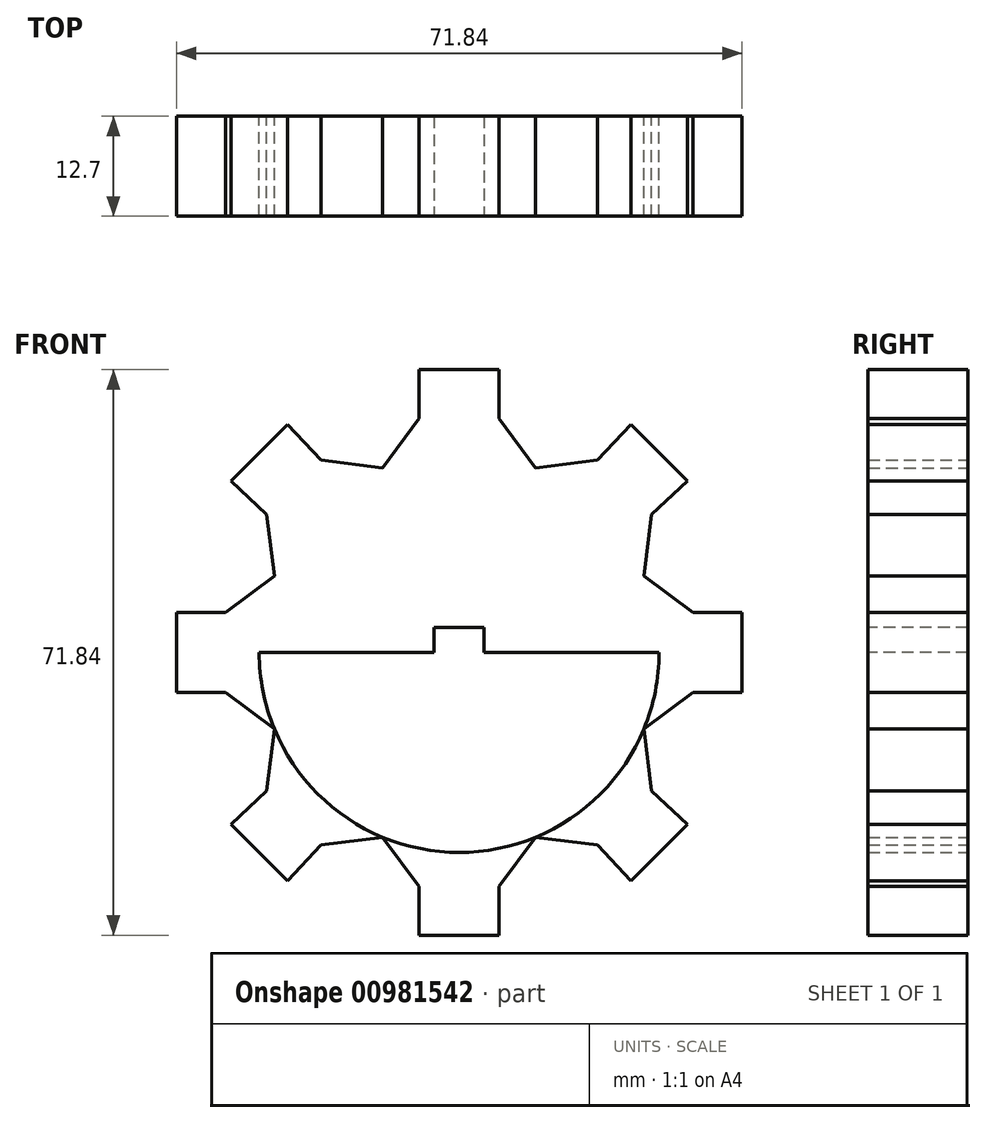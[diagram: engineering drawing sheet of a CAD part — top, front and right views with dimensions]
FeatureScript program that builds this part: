
annotation { "Feature Type Name" : "Feature", "Feature Type Description" : "" }
export const myFeature = defineFeature(function(context is Context, id is Id, definition is map)
    precondition{}
    {
        {
            var Q0;
            Q0=qCreatedBy(makeId("Front.planeOp"),FACE);
            var sketch = newSketch(context, id + "F0", { "sketchPlane" : qUnion([Q0])});
            skCircle(sketch, "E0", {"center": v(0, 0) * mm, "radius": 25.4 * mm});
            skLineSegment(sketch, "E1.bottom", {"start": v(0, 0) * mm, "end": v(-25.4, 0) * mm});
            skLineSegment(sketch, "E1.left", {"start": v(0, 0) * mm, "end": v(0, 25.4) * mm});
            skLineSegment(sketch, "E2", {"start": v(-25.4, 0) * mm, "end": v(-35.92, 0) * mm});
            skLineSegment(sketch, "E3", {"start": v(0, 25.4) * mm, "end": v(0, 35.92) * mm});
            skLineSegment(sketch, "E4", {"start": v(0, 35.92) * mm, "end": v(-5.08, 35.92) * mm});
            skPoint(sketch, "E5.endSnap0", {"position": v(-5.08, 29.7) * mm});
            skLineSegment(sketch, "E6", {"start": v(-25.4, 25.4) * mm, "end": v(-21.8, 29) * mm});
            skLineSegment(sketch, "E7", {"start": v(-21.8, 29) * mm, "end": v(-17.56, 24.43) * mm});
            skLineSegment(sketch, "E8", {"start": v(-25.4, 25.4) * mm, "end": v(-29, 21.8) * mm});
            skLineSegment(sketch, "E9", {"start": v(-29, 21.8) * mm, "end": v(-24.43, 17.56) * mm});
            skLineSegment(sketch, "E10", {"start": v(-35.92, 0) * mm, "end": v(-35.92, 5.08) * mm});
            skLineSegment(sketch, "E11", {"start": v(-35.92, 5.08) * mm, "end": v(-29.7, 5.08) * mm});
            skPoint(sketch, "E11.endSnap0", {"position": v(-29.7, 4.86) * mm});
            skLineSegment(sketch, "E12", {"start": v(-9.72, 23.47) * mm, "end": v(-17.56, 24.43) * mm});
            skLineSegment(sketch, "E13", {"start": v(-24.43, 17.56) * mm, "end": v(-23.47, 9.72) * mm});
            skLineSegment(sketch, "E14", {"start": v(-9.72, 23.47) * mm, "end": v(-5.08, 29.7) * mm});
            skLineSegment(sketch, "E15", {"start": v(-5.08, 29.7) * mm, "end": v(-5.08, 35.92) * mm});
            skLineSegment(sketch, "E16", {"start": v(-23.47, 9.72) * mm, "end": v(-29.7, 5.08) * mm});
            skLineSegment(sketch, "E17.1.0", {"start": v(25.4, 0) * mm, "end": v(35.92, 0) * mm});
            skLineSegment(sketch, "E17.1.1", {"start": v(23.47, 9.72) * mm, "end": v(24.43, 17.56) * mm});
            skLineSegment(sketch, "E17.1.2", {"start": v(35.92, 0) * mm, "end": v(35.92, 5.08) * mm});
            skLineSegment(sketch, "E17.1.3", {"start": v(9.72, 23.47) * mm, "end": v(5.08, 29.7) * mm});
            skLineSegment(sketch, "E17.1.4", {"start": v(17.56, 24.43) * mm, "end": v(9.72, 23.47) * mm});
            skLineSegment(sketch, "E17.1.5", {"start": v(29, 21.8) * mm, "end": v(24.43, 17.56) * mm});
            skLineSegment(sketch, "E17.1.6", {"start": v(29.7, 5.08) * mm, "end": v(35.92, 5.08) * mm});
            skLineSegment(sketch, "E17.1.7", {"start": v(23.47, 9.72) * mm, "end": v(29.7, 5.08) * mm});
            skPoint(sketch, "E17.1.8", {"position": v(4.86, 29.7) * mm});
            skLineSegment(sketch, "E17.1.10", {"start": v(0, 0) * mm, "end": v(25.4, 0) * mm});
            skLineSegment(sketch, "E17.1.11", {"start": v(5.08, 35.92) * mm, "end": v(5.08, 29.7) * mm});
            skPoint(sketch, "E17.1.12", {"position": v(29.7, 5.08) * mm});
            skLineSegment(sketch, "E17.1.13", {"start": v(21.8, 29) * mm, "end": v(17.56, 24.43) * mm});
            skLineSegment(sketch, "E17.1.15", {"start": v(25.4, 25.4) * mm, "end": v(29, 21.8) * mm});
            skLineSegment(sketch, "E17.1.16", {"start": v(0, 35.92) * mm, "end": v(5.08, 35.92) * mm});
            skLineSegment(sketch, "E17.1.17", {"start": v(25.4, 25.4) * mm, "end": v(21.8, 29) * mm});
            skLineSegment(sketch, "E17.2.0", {"start": v(0, -25.4) * mm, "end": v(0, -35.92) * mm});
            skLineSegment(sketch, "E17.2.1", {"start": v(9.72, -23.47) * mm, "end": v(17.56, -24.43) * mm});
            skLineSegment(sketch, "E17.2.2", {"start": v(0, -35.92) * mm, "end": v(5.08, -35.92) * mm});
            skLineSegment(sketch, "E17.2.3", {"start": v(23.47, -9.72) * mm, "end": v(29.7, -5.08) * mm});
            skLineSegment(sketch, "E17.2.4", {"start": v(24.43, -17.56) * mm, "end": v(23.47, -9.72) * mm});
            skLineSegment(sketch, "E17.2.5", {"start": v(21.8, -29) * mm, "end": v(17.56, -24.43) * mm});
            skLineSegment(sketch, "E17.2.6", {"start": v(5.08, -29.7) * mm, "end": v(5.08, -35.92) * mm});
            skLineSegment(sketch, "E17.2.7", {"start": v(9.72, -23.47) * mm, "end": v(5.08, -29.7) * mm});
            skPoint(sketch, "E17.2.8", {"position": v(29.7, -4.86) * mm});
            skLineSegment(sketch, "E17.2.9", {"start": v(0, 0) * mm, "end": v(25.4, 0) * mm});
            skLineSegment(sketch, "E17.2.10", {"start": v(0, 0) * mm, "end": v(0, -25.4) * mm});
            skLineSegment(sketch, "E17.2.11", {"start": v(35.92, -5.08) * mm, "end": v(29.7, -5.08) * mm});
            skPoint(sketch, "E17.2.12", {"position": v(5.08, -29.7) * mm});
            skLineSegment(sketch, "E17.2.13", {"start": v(29, -21.8) * mm, "end": v(24.43, -17.56) * mm});
            skLineSegment(sketch, "E17.2.14", {"start": v(25.4, 0) * mm, "end": v(35.92, 0) * mm});
            skLineSegment(sketch, "E17.2.15", {"start": v(25.4, -25.4) * mm, "end": v(21.8, -29) * mm});
            skLineSegment(sketch, "E17.2.16", {"start": v(35.92, 0) * mm, "end": v(35.92, -5.08) * mm});
            skLineSegment(sketch, "E17.2.17", {"start": v(25.4, -25.4) * mm, "end": v(29, -21.8) * mm});
            skLineSegment(sketch, "E17.3.1", {"start": v(-23.47, -9.72) * mm, "end": v(-24.43, -17.56) * mm});
            skLineSegment(sketch, "E17.3.2", {"start": v(-35.92, 0) * mm, "end": v(-35.92, -5.08) * mm});
            skLineSegment(sketch, "E17.3.3", {"start": v(-9.72, -23.47) * mm, "end": v(-5.08, -29.7) * mm});
            skLineSegment(sketch, "E17.3.4", {"start": v(-17.56, -24.43) * mm, "end": v(-9.72, -23.47) * mm});
            skLineSegment(sketch, "E17.3.5", {"start": v(-29, -21.8) * mm, "end": v(-24.43, -17.56) * mm});
            skLineSegment(sketch, "E17.3.6", {"start": v(-29.7, -5.08) * mm, "end": v(-35.92, -5.08) * mm});
            skLineSegment(sketch, "E17.3.7", {"start": v(-23.47, -9.72) * mm, "end": v(-29.7, -5.08) * mm});
            skPoint(sketch, "E17.3.8", {"position": v(-4.86, -29.7) * mm});
            skLineSegment(sketch, "E17.3.9", {"start": v(0, 0) * mm, "end": v(0, -25.4) * mm});
            skLineSegment(sketch, "E17.3.11", {"start": v(-5.08, -35.92) * mm, "end": v(-5.08, -29.7) * mm});
            skPoint(sketch, "E17.3.12", {"position": v(-29.7, -5.08) * mm});
            skLineSegment(sketch, "E17.3.13", {"start": v(-21.8, -29) * mm, "end": v(-17.56, -24.43) * mm});
            skLineSegment(sketch, "E17.3.14", {"start": v(0, -25.4) * mm, "end": v(0, -35.92) * mm});
            skLineSegment(sketch, "E17.3.15", {"start": v(-25.4, -25.4) * mm, "end": v(-29, -21.8) * mm});
            skLineSegment(sketch, "E17.3.16", {"start": v(0, -35.92) * mm, "end": v(-5.08, -35.92) * mm});
            skLineSegment(sketch, "E17.3.17", {"start": v(-25.4, -25.4) * mm, "end": v(-21.8, -29) * mm});
            skLineSegment(sketch, "E17.anchor1", {"start": v(0, 0) * mm, "end": v(-35.92, 0) * mm, "construction": true});
            skLineSegment(sketch, "E17.anchor2", {"start": v(0, 0) * mm, "end": v(0, -35.92) * mm, "construction": true});
            skSolve(sketch);
        }
        {
            var Q0;
            Q0=makeQuery(id+"F0.imprint","IMPRINT",FACE,{"disambiguationData":[TD([[makeQuery(id+"F0.imprint","IMPRINT",EDGE,{"derivedFrom":sQuery(id+"F0.wireOp",EDGE,"E4")}),1.0]])]});
            var Q1;
            {var subQ1=sQuery(id+"F0.wireOp",EDGE,"E17.1.3");Q1=makeQuery(id+"F0.imprint","IMPRINT",FACE,{"disambiguationData":[TD([[makeQuery(id+"F0.imprint","IMPRINT",EDGE,{"derivedFrom":subQ1}),1.0]])]});}
            var Q2;
            {var subQ1=sQuery(id+"F0.wireOp",EDGE,"E17.1.1");Q2=makeQuery(id+"F0.imprint","IMPRINT",FACE,{"disambiguationData":[TD([[makeQuery(id+"F0.imprint","IMPRINT",EDGE,{"derivedFrom":subQ1}),1.0]])]});}
            var Q3;
            Q3=makeQuery(id+"F0.imprint","IMPRINT",FACE,{"disambiguationData":[TD([[makeQuery(id+"F0.imprint","IMPRINT",EDGE,{"derivedFrom":sQuery(id+"F0.wireOp",EDGE,"E17.1.2")}),1.0]])]});
            var Q4;
            {var subQ1=sQuery(id+"F0.wireOp",EDGE,"E17.2.3");Q4=makeQuery(id+"F0.imprint","IMPRINT",FACE,{"disambiguationData":[TD([[makeQuery(id+"F0.imprint","IMPRINT",EDGE,{"derivedFrom":subQ1}),1.0]])]});}
            var Q5;
            {var subQ1=sQuery(id+"F0.wireOp",EDGE,"E17.2.1");Q5=makeQuery(id+"F0.imprint","IMPRINT",FACE,{"disambiguationData":[TD([[makeQuery(id+"F0.imprint","IMPRINT",EDGE,{"derivedFrom":subQ1}),1.0]])]});}
            var Q6;
            Q6=makeQuery(id+"F0.imprint","IMPRINT",FACE,{"disambiguationData":[TD([[makeQuery(id+"F0.imprint","IMPRINT",EDGE,{"derivedFrom":sQuery(id+"F0.wireOp",EDGE,"E17.2.2")}),1.0]])]});
            var Q7;
            {var subQ1=sQuery(id+"F0.wireOp",EDGE,"E17.3.3");Q7=makeQuery(id+"F0.imprint","IMPRINT",FACE,{"disambiguationData":[TD([[makeQuery(id+"F0.imprint","IMPRINT",EDGE,{"derivedFrom":subQ1}),1.0]])]});}
            var Q8;
            {var subQ1=sQuery(id+"F0.wireOp",EDGE,"E17.3.1");Q8=makeQuery(id+"F0.imprint","IMPRINT",FACE,{"disambiguationData":[TD([[makeQuery(id+"F0.imprint","IMPRINT",EDGE,{"derivedFrom":subQ1}),1.0]])]});}
            var Q9;
            {var subQ0=sQuery(id+"F0.wireOp",EDGE,"E2");Q9=makeQuery(id+"F0.imprint","IMPRINT",FACE,{"disambiguationData":[TD([[makeQuery(id+"F0.imprint","IMPRINT",EDGE,{"derivedFrom":subQ0}),1.0]])]});}
            var Q10;
            Q10=makeQuery(id+"F0.imprint","IMPRINT",FACE,{"disambiguationData":[TD([[makeQuery(id+"F0.imprint","IMPRINT",EDGE,{"derivedFrom":sQuery(id+"F0.wireOp",EDGE,"E10")}),-1.0]])]});
            var Q11;
            Q11=makeQuery(id+"F0.imprint","IMPRINT",FACE,{"disambiguationData":[TD([[makeQuery(id+"F0.imprint","IMPRINT",EDGE,{"derivedFrom":sQuery(id+"F0.wireOp",EDGE,"E6")}),-1.0]])]});
            var Q12;
            {var subQ0=sQuery(id+"F0.wireOp",EDGE,"E1.left");Q12=makeQuery(id+"F0.imprint","IMPRINT",FACE,{"disambiguationData":[TD([[makeQuery(id+"F0.imprint","IMPRINT",EDGE,{"derivedFrom":subQ0}),1.0]])]});}
            var Q13;
            {var subQ2=sQuery(id+"F0.wireOp",EDGE,"E1.left");Q13=makeQuery(id+"F0.imprint","IMPRINT",FACE,{"disambiguationData":[TD([[makeQuery(id+"F0.imprint","IMPRINT",EDGE,{"derivedFrom":subQ2}),-1.0]])]});}
            var Q14;
            {var subQ2=sQuery(id+"F0.wireOp",EDGE,"E17.2.9");Q14=makeQuery(id+"F0.imprint","IMPRINT",FACE,{"disambiguationData":[TD([[makeQuery(id+"F0.imprint","IMPRINT",EDGE,{"derivedFrom":subQ2}),-1.0]])]});}
            var Q15;
            {var subQ0=sQuery(id+"F0.wireOp",EDGE,"E17.3.9");Q15=makeQuery(id+"F0.imprint","IMPRINT",FACE,{"disambiguationData":[TD([[makeQuery(id+"F0.imprint","IMPRINT",EDGE,{"derivedFrom":subQ0}),-1.0]])]});}
            extrude(context, id + "F1", {"entities" : qUnion([Q0, Q1, Q2, Q3, Q4, Q5, Q6, Q7, Q8, Q9, Q10, Q11, Q12, Q13, Q14, Q15]), "depth" : 12.7 * mm, "offsetDistance" : 25.4 * mm});
        }
        {
            var Q0;
            Q0=makeQuery(id+"F1.opExtrude","CAP_FACE",FACE,{"disambiguationData":[OSD([sQuery(id+"F0.wireOp",EDGE,"E4"),sQuery(id+"F0.wireOp",EDGE,"E6"),sQuery(id+"F0.wireOp",EDGE,"E7"),sQuery(id+"F0.wireOp",EDGE,"E8"),sQuery(id+"F0.wireOp",EDGE,"E9"),sQuery(id+"F0.wireOp",EDGE,"E10"),sQuery(id+"F0.wireOp",EDGE,"E11"),sQuery(id+"F0.wireOp",EDGE,"E12"),sQuery(id+"F0.wireOp",EDGE,"E13"),sQuery(id+"F0.wireOp",EDGE,"E14"),sQuery(id+"F0.wireOp",EDGE,"E15"),sQuery(id+"F0.wireOp",EDGE,"E16"),sQuery(id+"F0.wireOp",EDGE,"E17.1.1"),sQuery(id+"F0.wireOp",EDGE,"E17.1.2"),sQuery(id+"F0.wireOp",EDGE,"E17.1.3"),sQuery(id+"F0.wireOp",EDGE,"E17.1.4"),sQuery(id+"F0.wireOp",EDGE,"E17.1.5"),sQuery(id+"F0.wireOp",EDGE,"E17.1.6"),sQuery(id+"F0.wireOp",EDGE,"E17.1.7"),sQuery(id+"F0.wireOp",EDGE,"E17.1.11"),sQuery(id+"F0.wireOp",EDGE,"E17.1.13"),sQuery(id+"F0.wireOp",EDGE,"E17.1.15"),sQuery(id+"F0.wireOp",EDGE,"E17.1.16"),sQuery(id+"F0.wireOp",EDGE,"E17.1.17"),sQuery(id+"F0.wireOp",EDGE,"E17.2.1"),sQuery(id+"F0.wireOp",EDGE,"E17.2.2"),sQuery(id+"F0.wireOp",EDGE,"E17.2.3"),sQuery(id+"F0.wireOp",EDGE,"E17.2.4"),sQuery(id+"F0.wireOp",EDGE,"E17.2.5"),sQuery(id+"F0.wireOp",EDGE,"E17.2.6"),sQuery(id+"F0.wireOp",EDGE,"E17.2.7"),sQuery(id+"F0.wireOp",EDGE,"E17.2.11"),sQuery(id+"F0.wireOp",EDGE,"E17.2.13"),sQuery(id+"F0.wireOp",EDGE,"E17.2.15"),sQuery(id+"F0.wireOp",EDGE,"E17.2.16"),sQuery(id+"F0.wireOp",EDGE,"E17.2.17"),sQuery(id+"F0.wireOp",EDGE,"E17.3.1"),sQuery(id+"F0.wireOp",EDGE,"E17.3.2"),sQuery(id+"F0.wireOp",EDGE,"E17.3.3"),sQuery(id+"F0.wireOp",EDGE,"E17.3.4"),sQuery(id+"F0.wireOp",EDGE,"E17.3.5"),sQuery(id+"F0.wireOp",EDGE,"E17.3.6"),sQuery(id+"F0.wireOp",EDGE,"E17.3.7"),sQuery(id+"F0.wireOp",EDGE,"E17.3.11"),sQuery(id+"F0.wireOp",EDGE,"E17.3.13"),sQuery(id+"F0.wireOp",EDGE,"E17.3.15"),sQuery(id+"F0.wireOp",EDGE,"E17.3.16"),sQuery(id+"F0.wireOp",EDGE,"E17.3.17")])],"isStart":false});
            var sketch = newSketch(context, id + "F2", { "sketchPlane" : qUnion([Q0])});
            skLineSegment(sketch, "E18.bottom", {"start": v(3.17, -3.18) * mm, "end": v(-3.17, -3.17) * mm});
            skLineSegment(sketch, "E18.top", {"start": v(3.18, 3.17) * mm, "end": v(-3.17, 3.18) * mm});
            skLineSegment(sketch, "E18.left", {"start": v(3.17, -3.18) * mm, "end": v(3.17, 3.17) * mm});
            skLineSegment(sketch, "E18.right", {"start": v(-3.17, -3.17) * mm, "end": v(-3.17, 3.18) * mm});
            skLineSegment(sketch, "E19", {"start": v(0, 0) * mm, "end": v(3.17, 0) * mm});
            skLineSegment(sketch, "E20", {"start": v(0, 0) * mm, "end": v(0, 3.18) * mm});
            skLineSegment(sketch, "E21", {"start": v(0, 0) * mm, "end": v(-3.17, 0) * mm});
            skLineSegment(sketch, "E22", {"start": v(0, 0) * mm, "end": v(0, -3.17) * mm});
            skSolve(sketch);
        }
        {
            var Q0;
            Q0 = qSketchRegion(id + "F2", true);
            extrude(context, id + "F3", {"entities" : qUnion([Q0]), "operationType" : NewBodyOperationType.REMOVE, "oppositeDirection" : true, "depth" : 12.7 * mm, "offsetDistance" : 25.4 * mm});
        }
    });
